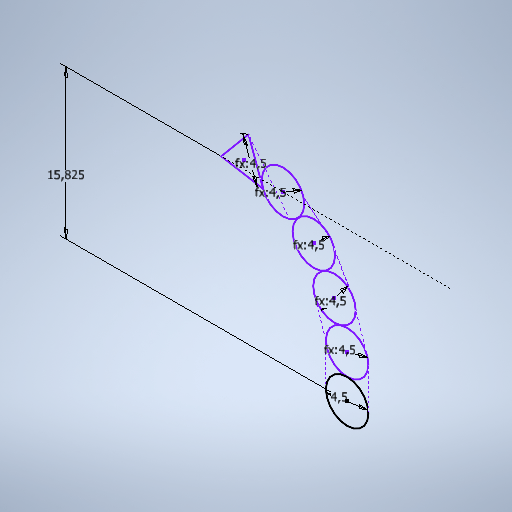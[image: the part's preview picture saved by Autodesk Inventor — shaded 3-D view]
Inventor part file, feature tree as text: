
AUTODESK INVENTOR PART (.ipt)
format: ipt  version: 2025.2 (Build 292293000, 293)  size: 274,944 bytes
history: native  units: mm
features: sketch x1
ambient origin geometry x8: Origin, YZ Plane, XZ Plane, XY Plane, X Axis, Y Axis, Z Axis, Center Point
feature tree (1):
  sketch  "Esboço1"  dims[d0=4.5mm d1=4.5mm d2=4.5mm d3=4.5mm d4=4.5mm d5=4.5mm d6=4.5mm d7=4.5mm d9=15.82528mm d11=4.5mm]
